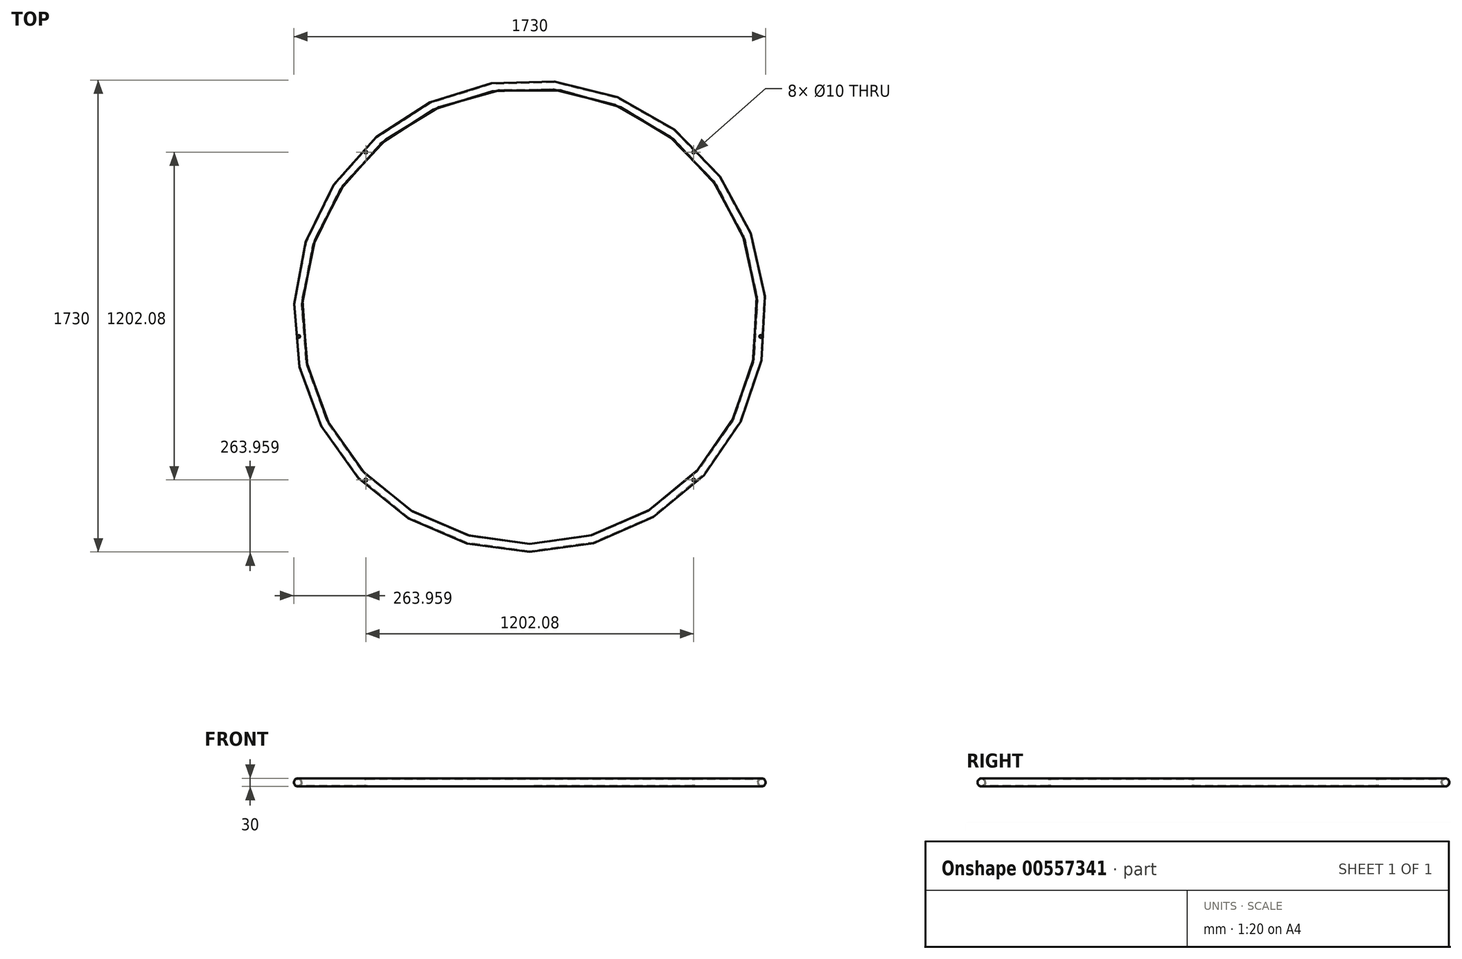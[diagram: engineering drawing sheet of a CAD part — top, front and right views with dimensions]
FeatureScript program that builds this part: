
annotation { "Feature Type Name" : "Feature", "Feature Type Description" : "" }
export const myFeature = defineFeature(function(context is Context, id is Id, definition is map)
    precondition{}
    {
        {
            var Q0;
            Q0=qCreatedBy(makeId("Front.planeOp"),FACE);
            var sketch = newSketch(context, id + "F0", { "sketchPlane" : qUnion([Q0])});
            skCircle(sketch, "E0", {"center": v(-850, 0) * mm, "radius": 15 * mm});
            skCircle(sketch, "E1", {"center": v(-850, 0) * mm, "radius": 12 * mm});
            skLineSegment(sketch, "E2", {"start": v(0, 0) * mm, "end": v(0, 380.17) * mm, "construction": true});
            skSolve(sketch);
        }
        {
            var Q0;
            Q0=qSketchRegion(id+"F0",true);
            var Q1;
            Q1=sQuery(id+"F0.wireOp",EDGE,"E2");
            revolve(context, id + "F1", {"entities" : qUnion([Q0]), "axis" : qUnion([Q1]), "revolveType" : RevolveType.ONE_DIRECTION, "angle" : 360 * degree});
        }
        {
            var Q0;
            Q0=qCreatedBy(makeId("Top.planeOp"),FACE);
            var sketch = newSketch(context, id + "F2", { "sketchPlane" : qUnion([Q0])});
            skArc(sketch, "E3", {"start": v(-850, 0) * mm, "mid": v(0, -850) * mm, "end": v(850, 0) * mm, "construction": true});
            skCircle(sketch, "E4", {"center": v(-846.68, -75) * mm, "radius": 5.25 * mm});
            skLineSegment(sketch, "E5", {"start": v(0, 0) * mm, "end": v(0, -850) * mm, "construction": true});
            skCircle(sketch, "E6.MirrorC", {"center": v(846.68, -75) * mm, "radius": 5.25 * mm});
            skSolve(sketch);
        }
        {
            var Q0;
            Q0=qSketchRegion(id+"F2",true);
            extrude(context, id + "F3", {"entities" : qUnion([Q0]), "operationType" : NewBodyOperationType.REMOVE, "endBound" : BoundingType.THROUGH_ALL, "oppositeDirection" : true, "depth" : 25 * mm, "offsetDistance" : 25 * mm, "hasSecondDirection" : true, "secondDirectionBound" : BoundingType.THROUGH_ALL, "secondDirectionOppositeDirection" : false, "secondDirectionDepth" : 25 * mm});
        }
        {
            var Q0;
            Q0=qCreatedBy(makeId("Top.planeOp"),FACE);
            var sketch = newSketch(context, id + "F4", { "sketchPlane" : qUnion([Q0])});
            skLineSegment(sketch, "E7", {"start": v(0, 0) * mm, "end": v(-601.04, -601.04) * mm, "construction": true});
            skCircle(sketch, "E8", {"center": v(-601.04, -601.04) * mm, "radius": 5 * mm});
            skCircle(sketch, "E9.1.0", {"center": v(601.04, -601.04) * mm, "radius": 5 * mm});
            skCircle(sketch, "E9.2.0", {"center": v(601.04, 601.04) * mm, "radius": 5 * mm});
            skCircle(sketch, "E9.3.0", {"center": v(-601.04, 601.04) * mm, "radius": 5 * mm});
            skPoint(sketch, "E9.center", {"position": v(0, 0) * mm});
            skSolve(sketch);
        }
        {
            var Q0;
            Q0 = qSketchRegion(id + "F4", true);
            extrude(context, id + "F5", {"entities" : qUnion([Q0]), "operationType" : NewBodyOperationType.REMOVE, "endBound" : BoundingType.THROUGH_ALL, "oppositeDirection" : true, "depth" : 25 * mm, "offsetDistance" : 25 * mm, "hasSecondDirection" : true, "secondDirectionBound" : BoundingType.THROUGH_ALL, "secondDirectionOppositeDirection" : false, "secondDirectionDepth" : 25 * mm});
        }
    });
